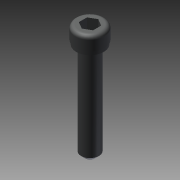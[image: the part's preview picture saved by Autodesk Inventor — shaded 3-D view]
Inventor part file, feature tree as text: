
AUTODESK INVENTOR PART (.ipt)
format: ipt  version: 2015 (Build 190159000, 159)  size: 118,272 bytes
history: native  units: in
note: dims shown in document units (in); Inventor stores cm internally (conversion verified against a paired STEP export)
features: other x6, extrude x1, chamfer x1, sketch x1
ambient origin geometry x8: Origin, YZ Plane, XZ Plane, XY Plane, X Axis, Y Axis, Z Axis, Center Point
bodies: Solid1 (feature_tree)
feature tree (9):
  other  "Screw 1.5in - 739195.ipt"
  extrude  "Extrusion1"  Depth=0.75in TaperAngle=0.0deg
  chamfer  "Chamfer1"  Distance=0.035in Angle=45.0deg
  other  "tetrix_739195_2013::Screw 1.5in - 739195.ipt"
  other  "TaggingFeature1"
  other  "FRONT"
  other  "TOP"
  other  "RIGHT"
  sketch  "Sketch1"  dims[d0=0.3937in d1=0.75in d2=0.0in d3=0.035in d4=0.125in d5=45.0deg]
